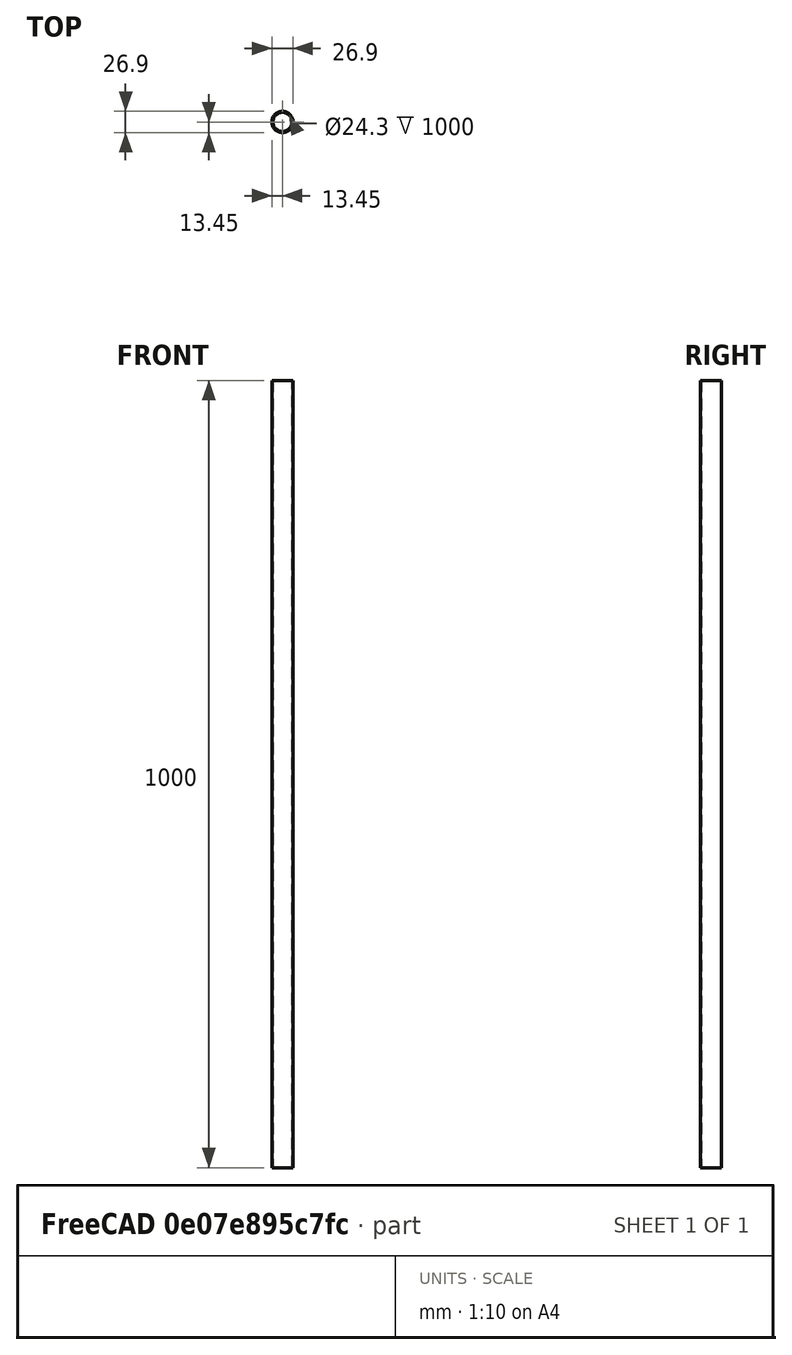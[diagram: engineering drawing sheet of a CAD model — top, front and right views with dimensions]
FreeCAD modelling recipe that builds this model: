
FCSTD DOCUMENT  (FreeCAD 0.21R33668 +26 (Git))
Label: pipe_3_4_inches
License: All rights reserved
LicenseURL: http://en.wikipedia.org/wiki/All_rights_reserved
objects: Sketcher::SketchObject×1, PartDesign::Pad×1, PartDesign::Body×1
note: 4 computed .brp shape members not serialized (recipe doc carries the construction recipe); baked Part::Feature solids carry a one-line shape summary decoded from their .brp

FEATURE [Sketcher::SketchObject] Sketch
  FullyConstrained = true
  MapMode = 5
  Support = -> [XY_Plane]
  sketch-geometry (2):
    g0: Circle CenterX=0 CenterY=0 CenterZ=0 NormalX=0 NormalY=0 NormalZ=1 AngleXU=0 Radius=13.45
    g1: Circle CenterX=0 CenterY=0 CenterZ=0 NormalX=0 NormalY=0 NormalZ=1 AngleXU=0 Radius=12.15
  constraints (4):
    c: Coincident(g0,g-1)
    c: Diameter(g0) = 26.9
    c: Coincident(g1,g0)
    c: Diameter(g1) = 24.3
FEATURE [PartDesign::Pad] Pad
  Direction = (0,0,1)
  Length = 1000
  Length2 = 10
  Profile = -> Sketch
  ReferenceAxis = -> Sketch [N_Axis]
  Type = 0
FEATURE [PartDesign::Body] Body
  Group = -> [Sketch,Pad]
  Origin = -> Origin
  Tip = -> Pad
